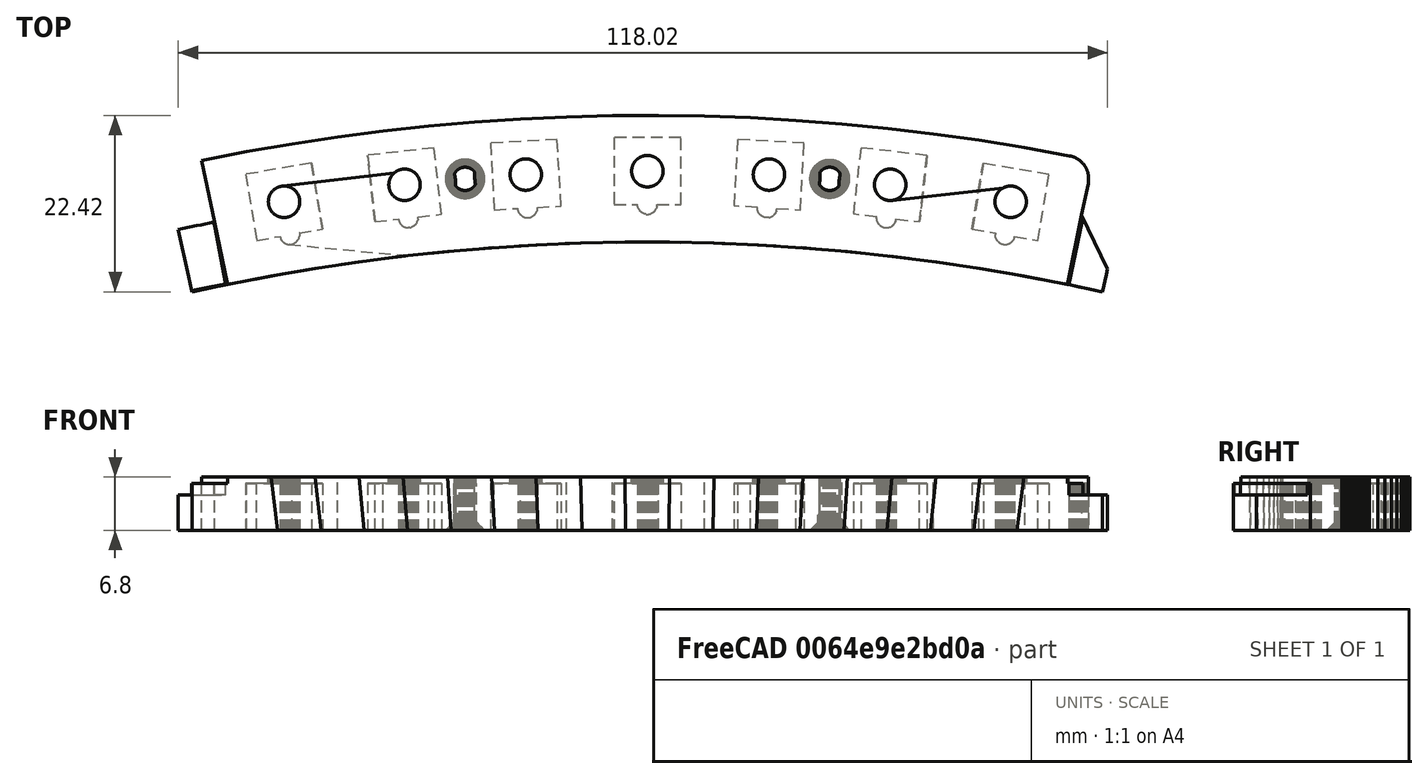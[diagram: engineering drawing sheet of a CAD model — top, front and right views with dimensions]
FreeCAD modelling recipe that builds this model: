
FCSTD DOCUMENT  (FreeCAD 0.21R33771 (Git))
Label: square_holes_thin_handles
License: All rights reserved
LicenseURL: http://en.wikipedia.org/wiki/All_rights_reserved
objects: Part::Box×2, Part::Cut×2, Part::Feature×1, Part::Common×1
note: 6 computed .brp shape members not serialized (recipe doc carries the construction recipe); baked Part::Feature solids carry a one-line shape summary decoded from their .brp

FEATURE [Part::Box] Box  label="Cube"
  AttacherType = Attacher::AttachEngine3D
  Height = 10
  Length = 10
  Placement = pos=(-63.3806,259.767,4.5) rot=(0,0,1;0.191986rad)
  Width = 10
FEATURE [Part::Box] Box001  label="Cube001"
  AttacherType = Attacher::AttachEngine3D
  Height = 10
  Length = 10
  Placement = pos=(53.2483,260.259,4.5) rot=(0,0,-1;0.20944rad)
  Width = 10
FEATURE [Part::Feature] square_holes001_solid  label="square_holes001 (Solid)"
  shape: bbox 118 x 22.42 x 6.8 mm, 22544 faces (baked)
FEATURE [Part::Cut] Cut
  Base = -> square_holes001_solid
  Tool = -> Box
FEATURE [Part::Cut] Cut001
  Base = -> square_holes001_solid
  Tool = -> Box001
FEATURE [Part::Common] Common
  Base = -> Cut
  Tool = -> Cut001
